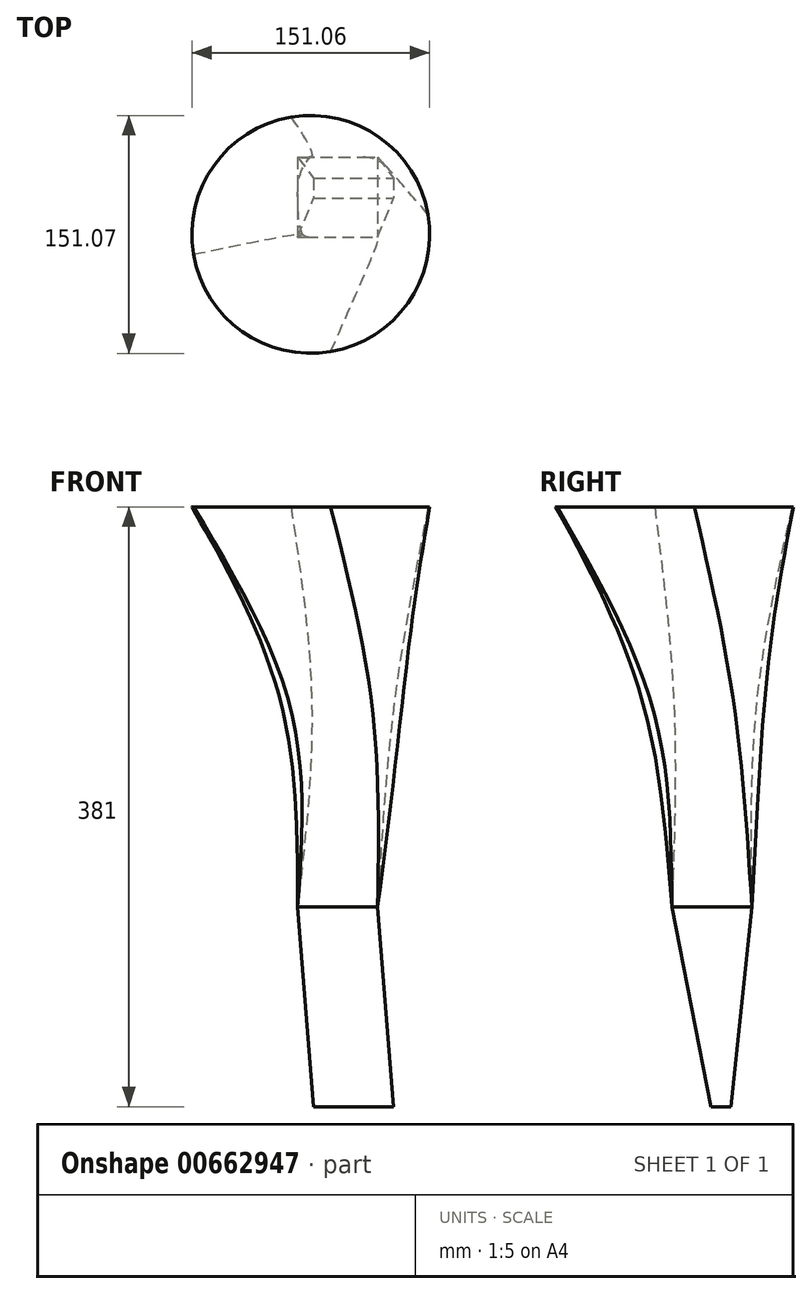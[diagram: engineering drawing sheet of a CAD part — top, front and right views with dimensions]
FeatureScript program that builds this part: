
annotation { "Feature Type Name" : "Feature", "Feature Type Description" : "" }
export const myFeature = defineFeature(function(context is Context, id is Id, definition is map)
    precondition{}
    {
        {
            var Q0;
            Q0=qCreatedBy(makeId("Top.planeOp"),FACE);
            cPlane(context, id + "F0", {"entities" : qUnion([Q0]), "cplaneType" : CPlaneType.OFFSET, "offset" : 76.2 * mm, "width" : 152.4 * mm, "height" : 152.4 * mm});
        }
        {
            var Q0;
            Q0=qCreatedBy(id+"F0.planeOp",FACE);
            cPlane(context, id + "F1", {"entities" : qUnion([Q0]), "cplaneType" : CPlaneType.OFFSET, "offset" : 127 * mm, "width" : 152.4 * mm, "height" : 152.4 * mm});
        }
        {
            var Q0;
            Q0=qCreatedBy(id+"F1.planeOp",FACE);
            cPlane(context, id + "F2", {"entities" : qUnion([Q0]), "cplaneType" : CPlaneType.OFFSET, "offset" : 127 * mm, "width" : 152.4 * mm, "height" : 152.4 * mm});
        }
        {
            var Q0;
            Q0=qCreatedBy(id+"F2.planeOp",FACE);
            var sketch = newSketch(context, id + "F3", { "sketchPlane" : qUnion([Q0])});
            skCircle(sketch, "E0", {"center": v(0, 0) * mm, "radius": 38.1 * mm});
            skSolve(sketch);
        }
        {
            var Q0;
            Q0=qCreatedBy(id+"F1.planeOp",FACE);
            var sketch = newSketch(context, id + "F4", { "sketchPlane" : qUnion([Q0])});
            skLineSegment(sketch, "E1.bottom", {"start": v(-28.03, 30.26) * mm, "end": v(22.77, 30.26) * mm});
            skLineSegment(sketch, "E1.top", {"start": v(-28.03, -20.54) * mm, "end": v(22.77, -20.54) * mm});
            skLineSegment(sketch, "E1.left", {"start": v(-28.03, 30.26) * mm, "end": v(-28.03, -20.54) * mm});
            skLineSegment(sketch, "E1.right", {"start": v(22.77, 30.26) * mm, "end": v(22.77, -20.54) * mm});
            skSolve(sketch);
        }
        {
            var Q0;
            Q0=qCreatedBy(id+"F0.planeOp",FACE);
            var sketch = newSketch(context, id + "F5", { "sketchPlane" : qUnion([Q0])});
            skLineSegment(sketch, "E2.bottom", {"start": v(-17.84, 16.98) * mm, "end": v(32.96, 16.98) * mm});
            skLineSegment(sketch, "E2.top", {"start": v(-17.84, 4.28) * mm, "end": v(32.96, 4.28) * mm});
            skLineSegment(sketch, "E2.left", {"start": v(-17.84, 16.98) * mm, "end": v(-17.84, 4.28) * mm});
            skLineSegment(sketch, "E2.right", {"start": v(32.96, 16.98) * mm, "end": v(32.96, 4.28) * mm});
            skSolve(sketch);
        }
        {
            var Q0;
            Q0=qCreatedBy(id+"F2.planeOp",FACE);
            cPlane(context, id + "F6", {"entities" : qUnion([Q0]), "cplaneType" : CPlaneType.OFFSET, "offset" : 127 * mm, "width" : 152.4 * mm, "height" : 152.4 * mm});
        }
        {
            var Q0;
            Q0=qCreatedBy(id+"F6.planeOp",FACE);
            var sketch = newSketch(context, id + "F7", { "sketchPlane" : qUnion([Q0])});
            skCircle(sketch, "E3", {"center": v(-19.71, -18.74) * mm, "radius": 75.53 * mm});
            skSolve(sketch);
        }
        {
            var Q0;
            Q0=makeQuery(id+"F7.imprint","IMPRINT",FACE,{"disambiguationData":[TD([[makeQuery(id+"F7.imprint","IMPRINT",EDGE,{"derivedFrom":sQuery(id+"F7.wireOp",EDGE,"E3")}),1.0]])]});
            var Q1;
            Q1=makeQuery(id+"F3.imprint","IMPRINT",FACE,{"disambiguationData":[TD([[makeQuery(id+"F3.imprint","IMPRINT",EDGE,{"derivedFrom":sQuery(id+"F3.wireOp",EDGE,"E0")}),1.0]])]});
            var Q2;
            Q2=makeQuery(id+"F4.imprint","IMPRINT",FACE,{"disambiguationData":[TD([[makeQuery(id+"F4.imprint","IMPRINT",EDGE,{"derivedFrom":sQuery(id+"F4.wireOp",EDGE,"E1.bottom")}),-1.0]])]});
            loft(context, id + "F8", {"sheetProfilesArray" : [{ "sheetProfileEntities" : qUnion([Q0]) }, { "sheetProfileEntities" : qUnion([Q1]) }, { "sheetProfileEntities" : qUnion([Q2]) }]});
        }
        {
            var Q0;
            Q0=makeQuery(id+"F4.imprint","IMPRINT",FACE,{"disambiguationData":[TD([[makeQuery(id+"F4.imprint","IMPRINT",EDGE,{"derivedFrom":sQuery(id+"F4.wireOp",EDGE,"E1.bottom")}),-1.0]])]});
            var Q1;
            Q1=makeQuery(id+"F5.imprint","IMPRINT",FACE,{"disambiguationData":[TD([[makeQuery(id+"F5.imprint","IMPRINT",EDGE,{"derivedFrom":sQuery(id+"F5.wireOp",EDGE,"E2.bottom")}),-1.0]])]});
            loft(context, id + "F9", {"sheetProfilesArray" : [{ "sheetProfileEntities" : qUnion([Q0]) }, { "sheetProfileEntities" : qUnion([Q1]) }]});
        }
        {
            var Q1;
            Q1=makeQuery(id+"F4.imprint","IMPRINT",FACE,{"disambiguationData":[TD([[makeQuery(id+"F4.imprint","IMPRINT",EDGE,{"derivedFrom":sQuery(id+"F4.wireOp",EDGE,"E1.bottom")}),-1.0]])]});
            var Q2;
            Q2=makeQuery(id+"F5.imprint","IMPRINT",FACE,{"disambiguationData":[TD([[makeQuery(id+"F5.imprint","IMPRINT",EDGE,{"derivedFrom":sQuery(id+"F5.wireOp",EDGE,"E2.bottom")}),-1.0]])]});
            loft(context, id + "F10", {"operationType" : NewBodyOperationType.ADD, "sheetProfilesArray" : [{ "sheetProfileEntities" : qUnion([Q1]) }, { "sheetProfileEntities" : qUnion([Q2]) }]});
        }
    });
